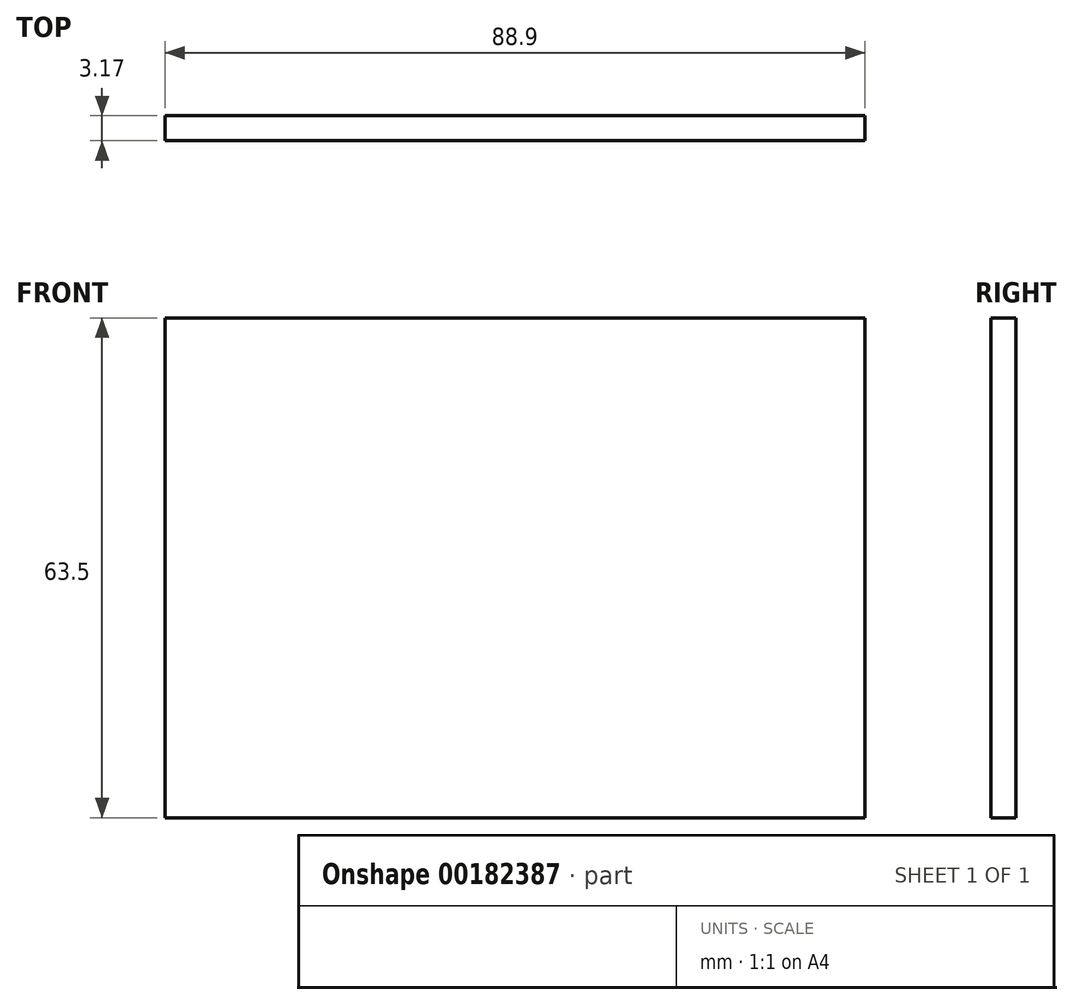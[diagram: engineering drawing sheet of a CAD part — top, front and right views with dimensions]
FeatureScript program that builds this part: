
annotation { "Feature Type Name" : "Feature", "Feature Type Description" : "" }
export const myFeature = defineFeature(function(context is Context, id is Id, definition is map)
    precondition{}
    {
        {
            var Q0;
            Q0=qCreatedBy(makeId("Front.planeOp"),FACE);
            var sketch = newSketch(context, id + "F0", { "sketchPlane" : qUnion([Q0])});
            skLineSegment(sketch, "E0.bottom", {"start": v(-37.97, 52.14) * mm, "end": v(50.93, 52.14) * mm});
            skLineSegment(sketch, "E0.top", {"start": v(-37.97, -11.36) * mm, "end": v(50.93, -11.36) * mm});
            skLineSegment(sketch, "E0.left", {"start": v(-37.97, 52.14) * mm, "end": v(-37.97, -11.36) * mm});
            skLineSegment(sketch, "E0.right", {"start": v(50.93, 52.14) * mm, "end": v(50.93, -11.36) * mm});
            skSolve(sketch);
        }
        {
            var Q0;
            Q0 = qSketchRegion(id + "F0", true);
            extrude(context, id + "F1", {"entities" : qUnion([Q0]), "depth" : 3.17 * mm});
        }
    });
